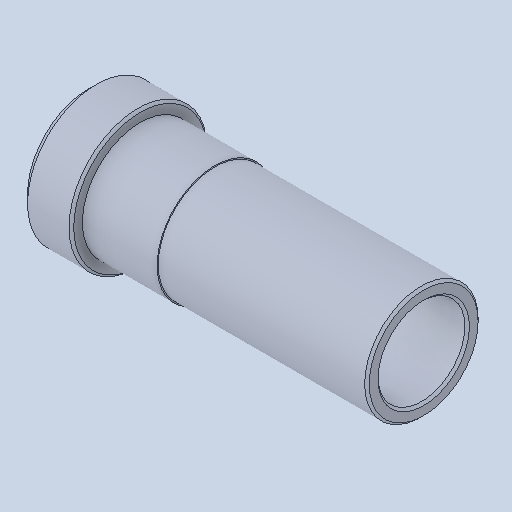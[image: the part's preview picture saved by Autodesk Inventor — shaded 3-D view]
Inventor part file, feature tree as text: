
AUTODESK INVENTOR PART (.ipt)
format: ipt  version: 2023 (Build 270158000, 158)  size: 135,168 bytes
history: native  units: in
note: dims shown in document units (in); Inventor stores cm internally (conversion verified against a paired STEP export)
features: chamfer x1
ambient origin geometry x8: Origin, YZ Plane, XZ Plane, XY Plane, X Axis, Y Axis, Z Axis, Center Point
bodies: Solid1 (feature_tree)
feature tree (1):
  chamfer  "Chamfer3"  [1 undecoded]
note: 1 required parameter value undecoded (feature->parameter linkage not recoverable at this tier; creation-order binding heuristic only, values carry confidence <= 0.55)
